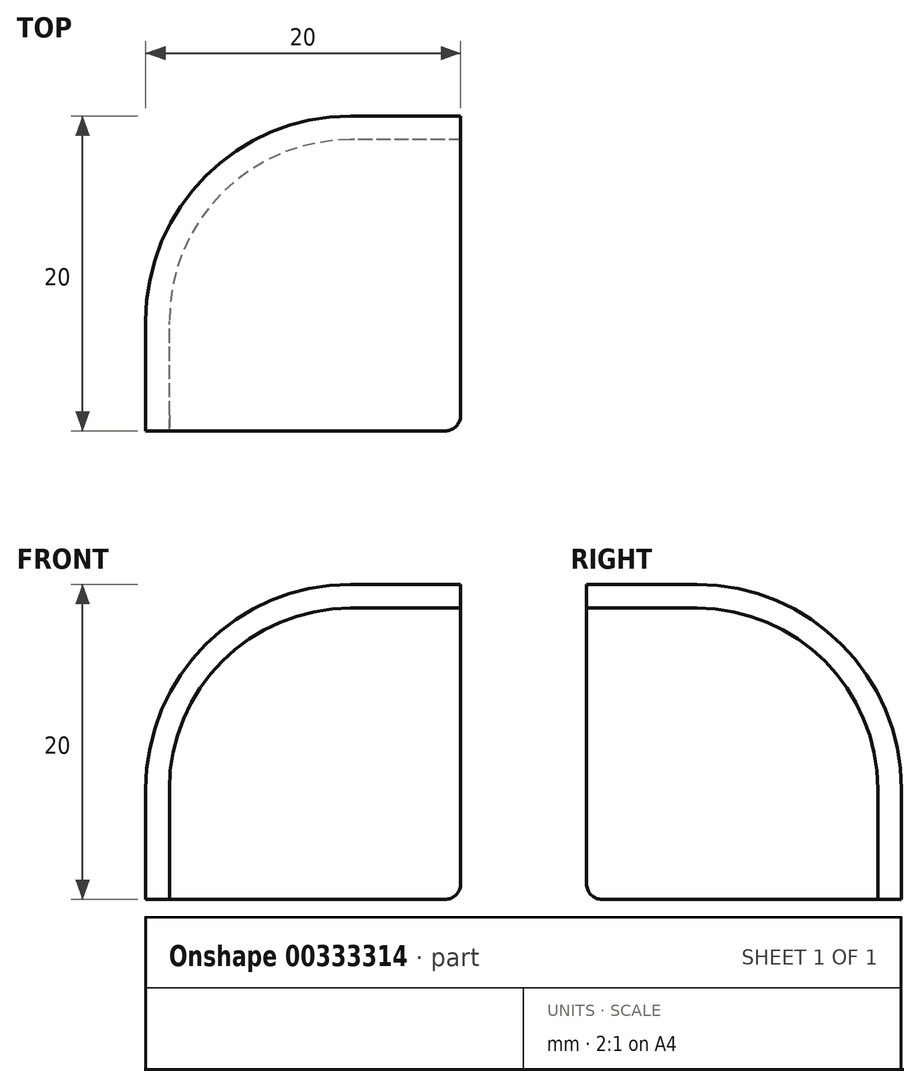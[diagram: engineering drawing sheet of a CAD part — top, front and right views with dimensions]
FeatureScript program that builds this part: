
annotation { "Feature Type Name" : "Feature", "Feature Type Description" : "" }
export const myFeature = defineFeature(function(context is Context, id is Id, definition is map)
    precondition{}
    {
        {
            var Q0;
            Q0=qCreatedBy(makeId("Top.planeOp"),FACE);
            var sketch = newSketch(context, id + "F0", { "sketchPlane" : qUnion([Q0])});
            skLineSegment(sketch, "E0.bottom", {"start": v(0, 0) * mm, "end": v(-13, 0) * mm});
            skLineSegment(sketch, "E0.top", {"start": v(0, 13) * mm, "end": v(0, 13) * mm});
            skLineSegment(sketch, "E0.left", {"start": v(0, 0) * mm, "end": v(0, 13) * mm});
            skLineSegment(sketch, "E0.right", {"start": v(-13, 0) * mm, "end": v(-13, 0) * mm});
            skPoint(sketch, "E1.visualSharp", {"position": v(-13, 13) * mm});
            skArc(sketch, "E1.filletArc", {"start": v(0, 13) * mm, "mid": v(-9.2, 9.2) * mm, "end": v(-13, 0) * mm});
            skSolve(sketch);
        }
        {
            var Q0;
            Q0=makeQuery(id+"F0.imprint","IMPRINT",FACE,{"disambiguationData":[TD([[makeQuery(id+"F0.imprint","IMPRINT",EDGE,{"derivedFrom":sQuery(id+"F0.wireOp",EDGE,"E0.bottom")}),-1.0]])]});
            var Q1;
            Q1=sQuery(id+"F0.wireOp",EDGE,"E0.left");
            revolve(context, id + "F1", {"entities" : qUnion([Q0]), "axis" : qUnion([Q1]), "revolveType" : RevolveType.ONE_DIRECTION, "angle" : 90 * degree});
        }
        {
            var Q0;
            Q0=makeQuery(id+"F1.opRevolve","CAP_FACE",FACE,{"disambiguationData":[OSD([sQuery(id+"F0.wireOp",EDGE,"E0.bottom"),sQuery(id+"F0.wireOp",EDGE,"E0.left"),sQuery(id+"F0.wireOp",EDGE,"E1.filletArc")])],"isStart":false});
            extrude(context, id + "F2", {"entities" : qUnion([Q0]), "operationType" : NewBodyOperationType.ADD, "depth" : 7 * mm});
        }
        {
            var Q0;
            {var subQ0=sQuery(id+"F0.wireOp",EDGE,"E0.left");Q0=makeQuery(id+"F2.boolean.opBoolean","MERGE",FACE,{"derivedFrom":[makeQuery(id+"F1.opRevolve","CAP_FACE",FACE,{"disambiguationData":[OSD([sQuery(id+"F0.wireOp",EDGE,"E0.bottom"),subQ0,sQuery(id+"F0.wireOp",EDGE,"E1.filletArc")])],"isStart":true}),makeQuery(id+"F2.opExtrude","SWEPT_FACE",FACE,{"disambiguationData":[OSD([subQ0])]})]});}
            extrude(context, id + "F3", {"entities" : qUnion([Q0]), "operationType" : NewBodyOperationType.ADD, "depth" : 7 * mm});
        }
        {
            var Q0;
            {var subQ0=sQuery(id+"F0.wireOp",EDGE,"E0.bottom");Q0=makeQuery(id+"F3.boolean.opBoolean","MERGE",FACE,{"derivedFrom":[makeQuery(id+"F2.boolean.opBoolean","MERGE",FACE,{"derivedFrom":[makeQuery(id+"F1.opRevolve","SWEPT_FACE",FACE,{"disambiguationData":[OSD([subQ0])]}),makeQuery(id+"F2.opExtrude","SWEPT_FACE",FACE,{"disambiguationData":[OSD([subQ0])]})]}),makeQuery(id+"F3.opExtrude","SWEPT_FACE",FACE,{"disambiguationData":[OSD([subQ0,sQuery(id+"F0.wireOp",EDGE,"E0.left")])]})]});}
            extrude(context, id + "F4", {"entities" : qUnion([Q0]), "operationType" : NewBodyOperationType.ADD, "depth" : 7 * mm});
        }
        {
            var Q0;
            {var subQ0=sQuery(id+"F0.wireOp",EDGE,"E0.left");var subQ1=sQuery(id+"F0.wireOp",EDGE,"E0.bottom");Q0=makeQuery(id+"F4.boolean.opBoolean","MERGE",FACE,{"derivedFrom":[makeQuery(id+"F3.boolean.opBoolean","MERGE",FACE,{"derivedFrom":[makeQuery(id+"F2.opExtrude","CAP_FACE",FACE,{"disambiguationData":[OSD([subQ1,subQ0,sQuery(id+"F0.wireOp",EDGE,"E1.filletArc")])],"isStart":false}),makeQuery(id+"F3.opExtrude","SWEPT_FACE",FACE,{"disambiguationData":[OSD([subQ0])]})]}),makeQuery(id+"F4.opExtrude","SWEPT_FACE",FACE,{"disambiguationData":[OSD([subQ1,subQ0]),TDD([makeQuery(id+"F3.boolean.opBoolean","MERGE",EDGE,{"derivedFrom":[makeQuery(id+"F2.opExtrude","CAP_EDGE",EDGE,{"disambiguationData":[OSD([subQ1])],"isStart":false}),makeQuery(id+"F3.opExtrude","SWEPT_EDGE",EDGE,{"disambiguationData":[OSD([subQ1,subQ0])]})]})])]})]});}
            var Q1;
            {var subQ0=sQuery(id+"F0.wireOp",EDGE,"E0.left");var subQ1=sQuery(id+"F0.wireOp",EDGE,"E0.bottom");Q1=makeQuery(id+"F4.boolean.opBoolean","MERGE",FACE,{"derivedFrom":[makeQuery(id+"F3.opExtrude","CAP_FACE",FACE,{"disambiguationData":[OSD([subQ1,subQ0,sQuery(id+"F0.wireOp",EDGE,"E1.filletArc")])],"isStart":false}),makeQuery(id+"F4.opExtrude","SWEPT_FACE",FACE,{"disambiguationData":[OSD([subQ1,subQ0]),TDD([makeQuery(id+"F3.opExtrude","CAP_EDGE",EDGE,{"disambiguationData":[OSD([subQ1,subQ0])],"isStart":false})])]})]});}
            var Q2;
            Q2=makeQuery(id+"F4.opExtrude","CAP_FACE",FACE,{"disambiguationData":[OSD([sQuery(id+"F0.wireOp",EDGE,"E0.bottom"),sQuery(id+"F0.wireOp",EDGE,"E0.left")])],"isStart":false});
            shell(context, id + "F5", {"entities" : qUnion([Q0, Q1, Q2]), "thickness" : 1.5 * mm});
        }
        {
            var Q0;
            {var subQ0=sQuery(id+"F0.wireOp",EDGE,"E0.left");var subQ1=sQuery(id+"F0.wireOp",EDGE,"E0.bottom");Q0=makeQuery(id+"F4.opExtrude","CAP_EDGE",EDGE,{"disambiguationData":[OSD([subQ1,subQ0]),TDD([makeQuery(id+"F3.boolean.opBoolean","MERGE",EDGE,{"derivedFrom":[makeQuery(id+"F2.opExtrude","CAP_EDGE",EDGE,{"disambiguationData":[OSD([subQ1])],"isStart":false}),makeQuery(id+"F3.opExtrude","SWEPT_EDGE",EDGE,{"disambiguationData":[OSD([subQ1,subQ0])]})]})])],"isStart":false});}
            var Q1;
            {var subQ0=sQuery(id+"F0.wireOp",EDGE,"E0.left");Q1=makeQuery(id+"F4.boolean.opBoolean","MERGE",EDGE,{"derivedFrom":[makeQuery(id+"F3.opExtrude","CAP_EDGE",EDGE,{"disambiguationData":[OSD([subQ0])],"isStart":false}),makeQuery(id+"F4.opExtrude","SWEPT_EDGE",EDGE,{"disambiguationData":[OSD([sQuery(id+"F0.wireOp",EDGE,"E0.bottom"),subQ0])]})]});}
            var Q2;
            {var subQ0=sQuery(id+"F0.wireOp",EDGE,"E0.left");var subQ1=sQuery(id+"F0.wireOp",EDGE,"E0.bottom");Q2=makeQuery(id+"F4.opExtrude","CAP_EDGE",EDGE,{"disambiguationData":[OSD([subQ1,subQ0]),TDD([makeQuery(id+"F3.opExtrude","CAP_EDGE",EDGE,{"disambiguationData":[OSD([subQ1,subQ0])],"isStart":false})])],"isStart":false});}
            fillet(context, id + "F6", {"entities" : qUnion([Q0, Q1, Q2]), "radius" : 1 * mm, "tangentPropagation" : true, "allowEdgeOverflow" : false});
        }
    });
